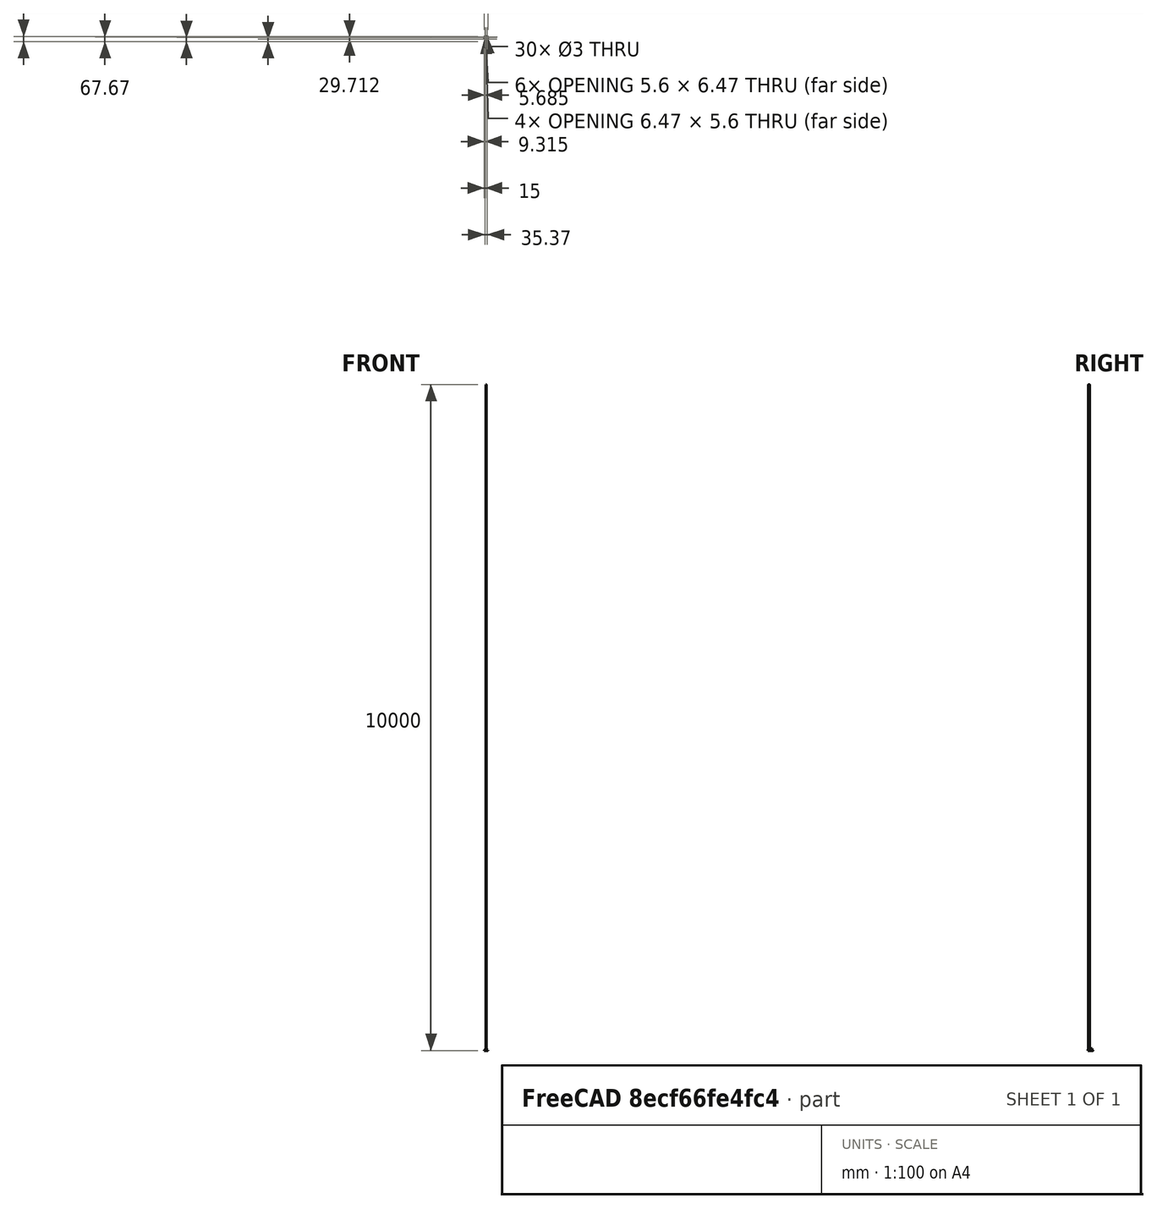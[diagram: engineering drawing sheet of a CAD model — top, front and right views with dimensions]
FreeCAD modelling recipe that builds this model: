
FCSTD DOCUMENT  (FreeCAD 0.16R6712 (Git))
Label: MotorMountV2
License: All rights reserved
LicenseURL: http://en.wikipedia.org/wiki/All_rights_reserved
objects: Sketcher::SketchObject×10, PartDesign::Pocket×6, PartDesign::Fillet×5, PartDesign::Pad×4, PartDesign::Mirrored×3, PartDesign::PolarPattern×2, App::DocumentObjectGroup×1, Mesh::Feature×1
note: 40 computed .brp shape members not serialized (recipe doc carries the construction recipe); baked Part::Feature solids carry a one-line shape summary decoded from their .brp

FEATURE [Sketcher::SketchObject] Sketch
  sketch-geometry (8):
    g0: ArcOfCircle CenterX=0 CenterY=0 CenterZ=0 NormalX=0 NormalY=0 NormalZ=1 Radius=22 StartAngle=5.10907 EndAngle=6.32168
    g1: LineSegment StartX=8.5 StartY=-20.2916 StartZ=0 EndX=8.5 EndY=-50 EndZ=0
    g2: LineSegment StartX=8.5 StartY=-50 StartZ=0 EndX=-8.5 EndY=-50 EndZ=0
    g3: LineSegment StartX=-8.5 StartY=-50 StartZ=0 EndX=-8.5 EndY=-20.2916 EndZ=0
    g4: ArcOfCircle CenterX=-12 CenterY=12.0416 CenterZ=0 NormalX=0 NormalY=0 NormalZ=1 Radius=15 StartAngle=0.724811 EndAngle=3.98412
    g5: ArcOfCircle CenterX=12 CenterY=12.0416 CenterZ=0 NormalX=0 NormalY=0 NormalZ=1 Radius=15 StartAngle=5.44066 EndAngle=8.69997
    g6: ArcOfCircle CenterX=0 CenterY=0 CenterZ=0 NormalX=0 NormalY=0 NormalZ=1 Radius=22 StartAngle=3.1031 EndAngle=4.3157
    g7: ArcOfCircle CenterX=0 CenterY=0 CenterZ=0 NormalX=0 NormalY=0 NormalZ=1 Radius=22 StartAngle=1.53576 EndAngle=1.60583
  constraints (28):
    c: Coincident(g0,g-1)
    c: Radius(g0) = 22
    c: Coincident(g1,g2)
    c: Coincident(g2,g3)
    c: Horizontal(g2)
    c: Vertical(g1)
    c: Vertical(g3)
    c: Coincident(g0,g1)
    c: Coincident(g6,g3)
    c: DistanceY(g3,g3) = 29.7084
    c: Distance(g2) = 17
    c: DistanceY(g1,g1) = 29.7084
    c: Radius(g4) = 15
    c: Radius(g5) = 15
    c: Distance(g-1,g5) = 17
    c: Distance(g-1,g4) = 17
    c: DistanceX(g4,g-1) = 12
    c: DistanceX(g-1,g5) = 12
    c: Equal(g0,g6)
    c: PointOnObject(g6,g4)
    c: Coincident(g0,g6)
    c: Coincident(g4,g7)
    c: Equal(g0,g7)
    c: Coincident(g0,g5)
    c: Coincident(g7,g5)
    c: Coincident(g0,g7)
    c: Symmetric(g5,g4,g-2)
    c: Symmetric(g0,g4,g-2)
FEATURE [PartDesign::Pad] Pad  label="Base"
  Length = 5
  Length2 = 100
  Sketch = -> Sketch
  Type = 0
FEATURE [Sketcher::SketchObject] Sketch001
  ExternalGeometry = -> [Pad]
  Placement = pos=(0,0,5) rot=(0,0,1;0rad)
  Support = -> Pad [Face10]
  sketch-geometry (4):
    g0: LineSegment StartX=-8.5 StartY=9.99998 StartZ=0 EndX=8.5 EndY=9.99998 EndZ=0
    g1: LineSegment StartX=8.5 StartY=9.99998 StartZ=0 EndX=8.5 EndY=-50 EndZ=0
    g2: LineSegment StartX=8.5 StartY=-50 StartZ=0 EndX=-8.5 EndY=-50 EndZ=0
    g3: LineSegment StartX=-8.5 StartY=-50 StartZ=0 EndX=-8.5 EndY=9.99998 EndZ=0
  constraints (11):
    c: Coincident(g0,g1)
    c: Coincident(g1,g2)
    c: Coincident(g2,g3)
    c: Coincident(g3,g0)
    c: Horizontal(g0)
    c: Horizontal(g2)
    c: Vertical(g1)
    c: Vertical(g3)
    c: DistanceX(g0,g0) = 17
    c: DistanceY(g3,g3) = 60
    c: Coincident(g-3,g1)
FEATURE [PartDesign::Pad] Pad001  label="Bloc_profil_alu"
  Length = 12
  Length2 = 100
  Sketch = -> Sketch001
  Type = 0
FEATURE [Sketcher::SketchObject] Sketch013
  ExternalGeometry = -> [Pad001]
  Placement = pos=(0,0,17) rot=(0,0,1;0rad)
  Support = -> Pad001 [Face14]
  sketch-geometry (4):
    g0: LineSegment StartX=-8.5 StartY=9.99998 StartZ=0 EndX=8.5 EndY=9.99998 EndZ=0
    g1: LineSegment StartX=8.5 StartY=9.99998 StartZ=0 EndX=8.5 EndY=-15 EndZ=0
    g2: LineSegment StartX=8.5 StartY=-15 StartZ=0 EndX=-8.5 EndY=-15 EndZ=0
    g3: LineSegment StartX=-8.5 StartY=-15 StartZ=0 EndX=-8.5 EndY=9.99998 EndZ=0
  constraints (11):
    c: Coincident(g1,g2)
    c: Coincident(g2,g3)
    c: Coincident(g3,g0)
    c: Horizontal(g0)
    c: Horizontal(g2)
    c: Vertical(g1)
    c: Vertical(g3)
    c: DistanceY(g3,g3) = 25
    c: DistanceX(g0,g0) = 17
    c: Coincident(g0,g1)
    c: Coincident(g0,g-3)
FEATURE [PartDesign::Pad] Pad002  label="Pied_atterissage"
  Length = 15
  Length2 = 100
  Sketch = -> Sketch013
  Type = 0
FEATURE [Sketcher::SketchObject] Sketch003
  Placement = pos=(0,0,0) rot=(1,0,0;3.14159rad)
  Support = -> Pad002 [Face4]
  sketch-geometry (1):
    g0: Circle CenterX=12 CenterY=-12.0416 CenterZ=0 NormalX=0 NormalY=0 NormalZ=1 Radius=1.5
  constraints (3):
    c: Distance(g-1,g0) = 17
    c: DistanceX(g-2,g0) = 12
    c: Radius(g0) = 1.5
FEATURE [PartDesign::Pocket] Pocket001  label="Percage_support_moteur"
  Length = 5
  Sketch = -> Sketch003
  Type = 1
FEATURE [PartDesign::PolarPattern] PolarPattern
  Angle = 360
  Axis = -> Sketch003 [N_Axis]
  Occurrences = 4
  Originals = -> [Pocket001]
FEATURE [Sketcher::SketchObject] Sketch004  label="Nut_pocket_support_moteur"
  Placement = pos=(0,0,5) rot=(0,0,1;0rad)
  Support = -> PolarPattern [Face5]
  sketch-geometry (7):
    g0: LineSegment StartX=14.8 StartY=10.3834 StartZ=0 EndX=14.8 EndY=13.6166 EndZ=0
    g1: LineSegment StartX=14.8 StartY=13.6166 StartZ=0 EndX=12 EndY=15.2332 EndZ=0
    g2: LineSegment StartX=12 StartY=15.2332 StartZ=0 EndX=9.2 EndY=13.6166 EndZ=0
    g3: LineSegment StartX=9.2 StartY=13.6166 StartZ=0 EndX=9.2 EndY=10.3834 EndZ=0
    g4: LineSegment StartX=9.2 StartY=10.3834 StartZ=0 EndX=12 EndY=8.76684 EndZ=0
    g5: LineSegment StartX=12 StartY=8.76684 StartZ=0 EndX=14.8 EndY=10.3834 EndZ=0
    g6: Circle [constr] CenterX=12 CenterY=12 CenterZ=0 NormalX=0 NormalY=0 NormalZ=1 Radius=3.23316
  constraints (17):
    c: Coincident(g0,g1)
    c: Coincident(g1,g2)
    c: Coincident(g2,g3)
    c: Coincident(g3,g4)
    c: Coincident(g4,g5)
    c: Coincident(g5,g0)
    c: Equal(g0, g1-g5) x5
    c: PointOnObject(g0,g6)
    c: PointOnObject(g1,g6)
    c: PointOnObject(g2,g6)
    c: PointOnObject(g3,g6)
    c: PointOnObject(g4,g6)
    c: PointOnObject(g5,g6)
    c: Vertical(g0)
    c: DistanceY(g-1,g6) = 12
    c: DistanceX(g-2,g6) = 12
    c: Distance(g3,g0) = 5.6
FEATURE [PartDesign::Pocket] Pocket002  label="Nut_pocket_support_moteur001"
  Length = 2
  Sketch = -> Sketch004
  Type = 0
FEATURE [PartDesign::PolarPattern] PolarPattern001  label="nut_pocketx4"
  Angle = 360
  Axis = -> Sketch004 [N_Axis]
  Occurrences = 4
  Originals = -> [Pocket002]
FEATURE [Sketcher::SketchObject] Sketch010
  Placement = pos=(0,0,5) rot=(0,0,1;0rad)
  Support = -> PolarPattern001 [Face5]
  sketch-geometry (2):
    g0: Circle CenterX=6.38516 CenterY=17.67 CenterZ=0 NormalX=0 NormalY=0 NormalZ=1 Radius=1.5
    g1: Circle CenterX=17.6852 CenterY=6.37 CenterZ=0 NormalX=0 NormalY=0 NormalZ=1 Radius=1.5
FEATURE [PartDesign::Pad] Pad003  label="lock_protect"
  Length = 2
  Length2 = 100
  Sketch = -> Sketch010
  Type = 0
FEATURE [PartDesign::Mirrored] Mirrored  label="lock_protect_sym"
  MirrorPlane = -> Sketch010 [V_Axis]
  Originals = -> [Pad003]
FEATURE [Sketcher::SketchObject] Sketch005
  Placement = pos=(0,0,5) rot=(0,0,1;0rad)
  Support = -> Mirrored [Face5]
  sketch-geometry (1):
    g0: Circle CenterX=17.6852 CenterY=17.67 CenterZ=0 NormalX=0 NormalY=0 NormalZ=1 Radius=1.5
  constraints (1):
    c: DistanceY(g-1,g0) = 17.67
FEATURE [PartDesign::Pocket] Pocket003  label="percage_protect"
  Length = 5
  Sketch = -> Sketch005
  Type = 1
FEATURE [PartDesign::Mirrored] Mirrored001  label="percage_protect_symetrie"
  MirrorPlane = -> Sketch005 [V_Axis]
  Originals = -> [Pocket003]
FEATURE [Sketcher::SketchObject] Sketch014
  ExternalGeometry = -> [Mirrored001]
  Placement = pos=(0,0,0) rot=(1,0,0;3.14159rad)
  Support = -> Mirrored001 [Face4]
  sketch-geometry (7):
    g0: LineSegment StartX=20.4852 StartY=-19.2866 StartZ=0 EndX=20.4852 EndY=-16.0534 EndZ=0
    g1: LineSegment StartX=20.4852 StartY=-16.0534 StartZ=0 EndX=17.6852 EndY=-14.4368 EndZ=0
    g2: LineSegment StartX=17.6852 StartY=-14.4368 StartZ=0 EndX=14.8852 EndY=-16.0534 EndZ=0
    g3: LineSegment StartX=14.8852 StartY=-16.0534 StartZ=0 EndX=14.8852 EndY=-19.2866 EndZ=0
    g4: LineSegment StartX=14.8852 StartY=-19.2866 StartZ=0 EndX=17.6852 EndY=-20.9032 EndZ=0
    g5: LineSegment StartX=17.6852 StartY=-20.9032 StartZ=0 EndX=20.4852 EndY=-19.2866 EndZ=0
    g6: Circle [constr] CenterX=17.6852 CenterY=-17.67 CenterZ=0 NormalX=0 NormalY=0 NormalZ=1 Radius=3.23316
  constraints (16):
    c: Coincident(g0,g1)
    c: Coincident(g1,g2)
    c: Coincident(g2,g3)
    c: Coincident(g3,g4)
    c: Coincident(g4,g5)
    c: Coincident(g5,g0)
    c: Equal(g0, g1-g5) x5
    c: PointOnObject(g0,g6)
    c: PointOnObject(g1,g6)
    c: PointOnObject(g2,g6)
    c: PointOnObject(g3,g6)
    c: PointOnObject(g4,g6)
    c: PointOnObject(g5,g6)
    c: Vertical(g0)
    c: Distance(g0,g3) = 5.6
    c: Coincident(g-3,g6)
FEATURE [PartDesign::Pocket] Pocket004  label="pocket_protect"
  Length = 2
  Sketch = -> Sketch014
  Type = 0
FEATURE [PartDesign::Mirrored] Mirrored002  label="pocket_protect_sym"
  MirrorPlane = -> Sketch014 [V_Axis]
  Originals = -> [Pocket004]
FEATURE [PartDesign::Fillet] Fillet
  Base = -> Mirrored002 [Edge11,Edge73,Edge112,Edge179,Edge71,Edge7]
  Radius = 1
FEATURE [PartDesign::Fillet] Fillet001
  Base = -> Fillet [Edge121,Edge193,Edge194,Edge36,Edge123,Edge125]
  Radius = 5
FEATURE [PartDesign::Fillet] Fillet002
  Base = -> Fillet001 [Edge165,Edge166,Edge142,Edge167,Edge54,Edge168,Edge164,Edge169]
  Radius = 3
FEATURE [Sketcher::SketchObject] Sketch015
  Placement = pos=(0,0,32) rot=(0,0,1;0rad)
  Support = -> Fillet002 [Face9]
  sketch-geometry (1):
    g0: Circle CenterX=0 CenterY=0 CenterZ=0 NormalX=0 NormalY=0 NormalZ=1 Radius=4
  constraints (2):
    c: Coincident(g0,g-1)
    c: Radius(g0) = 4
FEATURE [PartDesign::Pocket] Pocket005
  Length = 15
  Sketch = -> Sketch015
  Type = 0
FEATURE [PartDesign::Fillet] Fillet003
  Base = -> Pocket005 [Edge33]
  Radius = 1
FEATURE [PartDesign::Fillet] Fillet004
  Base = -> Fillet003 [Edge64,Edge68]
  Radius = 1
FEATURE [Sketcher::SketchObject] Sketch006
  Placement = pos=(0,0,0) rot=(1,0,0;3.14159rad)
  Support = -> Fillet004 [Face47]
  sketch-geometry (2):
    g0: Circle CenterX=0 CenterY=40 CenterZ=0 NormalX=0 NormalY=0 NormalZ=1 Radius=2
    g1: Circle CenterX=0 CenterY=30 CenterZ=0 NormalX=0 NormalY=0 NormalZ=1 Radius=2
  constraints (6):
    c: PointOnObject(g0,g-2)
    c: PointOnObject(g1,g-2)
    c: Equal(g1,g0)
    c: Radius(g0) = 2
    c: DistanceY(g-1,g1) = 30
    c: DistanceY(g1,g0) = 10
FEATURE [PartDesign::Pocket] Pocket
  Length = 5
  Sketch = -> Sketch006
  Type = 1
FEATURE [App::DocumentObjectGroup] Groupe
  Group = -> [Pad,Pad001,Pad002,Pocket001,PolarPattern,Pocket002,PolarPattern001,Pad003,Mirrored,Pocket003,Mirrored001,Pocket004,Mirrored002,Fillet,Fillet001,Fillet002,Pocket005,Fillet003,Fillet004,Pocket]
FEATURE [Mesh::Feature] Mesh  label="Pocket (Meshed)"
